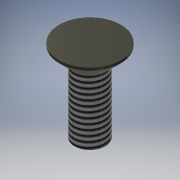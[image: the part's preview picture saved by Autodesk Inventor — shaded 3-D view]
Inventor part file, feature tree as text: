
AUTODESK INVENTOR PART (.ipt)
format: ipt  version: 2020.2 (Build 242310000, 310)  size: 124,928 bytes
history: native  units: mm
features: extrude x2, sketch x2, other x1, thread x1, chamfer x1
ambient origin geometry x1: Origin
bodies: Body1 (feature_tree)
feature tree (7):
  other  "ソリッド1"
  extrude  "押し出し1"  Depth=3.0mm
  extrude  "押し出し2"  Depth=6.25mm TaperAngle=0.0deg
  thread  "ねじ1"
  chamfer  "面取り1"  Distance=6.0mm
  sketch  "スケッチ1"
  sketch  "スケッチ2"
